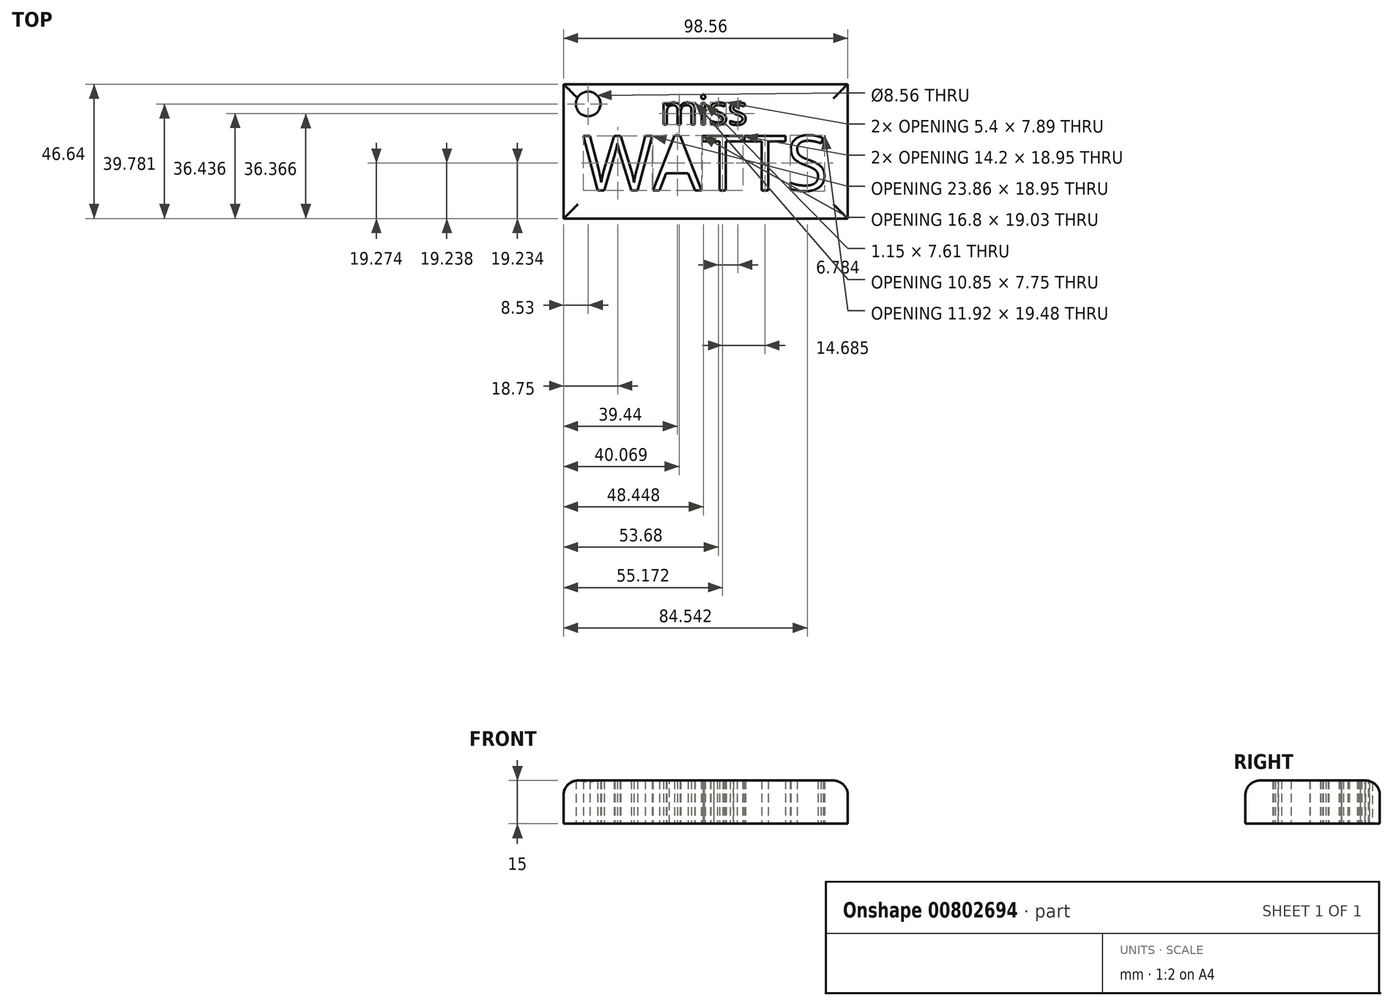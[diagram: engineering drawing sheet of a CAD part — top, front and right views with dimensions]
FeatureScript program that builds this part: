
annotation { "Feature Type Name" : "Feature", "Feature Type Description" : "" }
export const myFeature = defineFeature(function(context is Context, id is Id, definition is map)
    precondition{}
    {
        {
            var Q0;
            Q0=qCreatedBy(makeId("Top.planeOp"),FACE);
            var sketch = newSketch(context, id + "F0", { "sketchPlane" : qUnion([Q0])});
            skLineSegment(sketch, "E0.bottom", {"start": v(-55.64, 33.38) * mm, "end": v(42.92, 33.38) * mm});
            skLineSegment(sketch, "E0.top", {"start": v(-55.64, -13.26) * mm, "end": v(42.92, -13.26) * mm});
            skLineSegment(sketch, "E0.left", {"start": v(-55.64, 33.38) * mm, "end": v(-55.64, -13.26) * mm});
            skLineSegment(sketch, "E0.right", {"start": v(42.92, 33.38) * mm, "end": v(42.92, -13.26) * mm});
            skText(sketch, "E1", { "text": "WATTS", "fontName": "OpenSans-Regular.ttf"});
            skCircle(sketch, "E2", {"center": v(-47.11, 26.52) * mm, "radius": 4.28 * mm});
            skText(sketch, "E3", { "text": "miss", "fontName": "OpenSans-Regular.ttf"});
            const initialGuessF0  = {"E1": [-0.04917, -0.0035, 1, 0, 0.01911], "E3": [-0.02222, 0.0193, 1, 0, 0.01024]};
            skSetInitialGuess(sketch, initialGuessF0);
            skSolve(sketch);
        }
        {
            var Q0;
            Q0 = qSketchRegion(id + "F0", true);
            extrude(context, id + "F1", {"entities" : qUnion([Q0]), "depth" : 15 * mm, "offsetDistance" : 25 * mm});
        }
        {
            var Q0;
            Q0=makeQuery(id+"F1.opExtrude","CAP_EDGE",EDGE,{"disambiguationData":[OSD([sQuery(id+"F0.wireOp",EDGE,"E0.bottom")])],"isStart":false});
            var Q1;
            Q1=makeQuery(id+"F1.opExtrude","CAP_EDGE",EDGE,{"disambiguationData":[OSD([sQuery(id+"F0.wireOp",EDGE,"E0.left")])],"isStart":false});
            var Q2;
            Q2=makeQuery(id+"F1.opExtrude","CAP_EDGE",EDGE,{"disambiguationData":[OSD([sQuery(id+"F0.wireOp",EDGE,"E0.top")])],"isStart":false});
            var Q3;
            Q3=makeQuery(id+"F1.opExtrude","CAP_EDGE",EDGE,{"disambiguationData":[OSD([sQuery(id+"F0.wireOp",EDGE,"E0.right")])],"isStart":false});
            fillet(context, id + "F2", {"entities" : qUnion([Q0, Q1, Q2, Q3]), "radius" : 5 * mm, "tangentPropagation" : true, "allowEdgeOverflow" : false});
        }
    });
